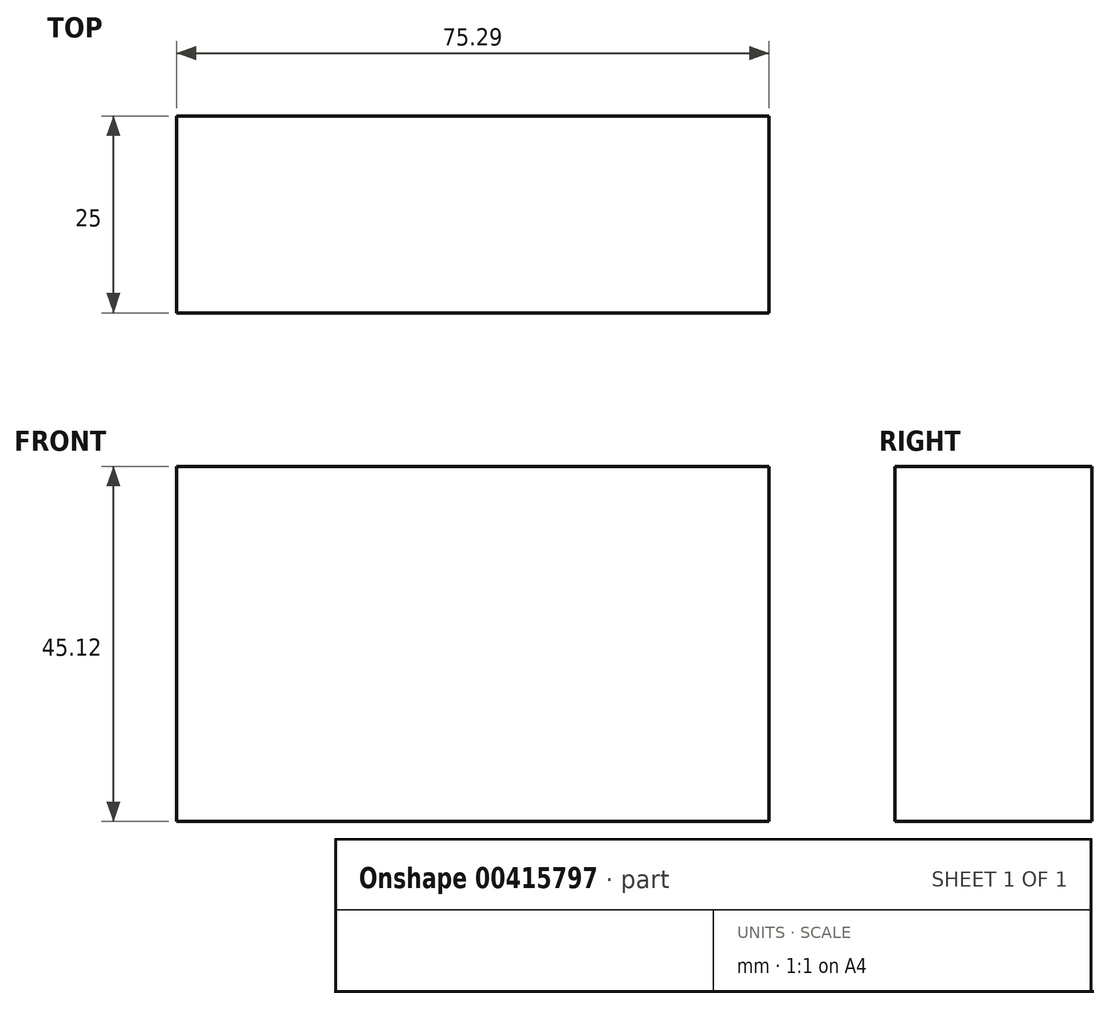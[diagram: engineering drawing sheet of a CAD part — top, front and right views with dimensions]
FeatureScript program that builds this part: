
annotation { "Feature Type Name" : "Feature", "Feature Type Description" : "" }
export const myFeature = defineFeature(function(context is Context, id is Id, definition is map)
    precondition{}
    {
        {
            var Q0;
            Q0=qCreatedBy(makeId("Front.planeOp"),FACE);
            var sketch = newSketch(context, id + "F0", { "sketchPlane" : qUnion([Q0])});
            skLineSegment(sketch, "E0.bottom", {"start": v(-100.61, 5.68) * mm, "end": v(-25.32, 5.68) * mm});
            skLineSegment(sketch, "E0.top", {"start": v(-100.61, -39.44) * mm, "end": v(-25.32, -39.44) * mm});
            skLineSegment(sketch, "E0.left", {"start": v(-100.61, 5.68) * mm, "end": v(-100.61, -39.44) * mm});
            skLineSegment(sketch, "E0.right", {"start": v(-25.32, 5.68) * mm, "end": v(-25.32, -39.44) * mm});
            skSolve(sketch);
        }
        {
            var Q0;
            Q0 = qSketchRegion(id + "F0", true);
            extrude(context, id + "F1", {"entities" : qUnion([Q0]), "depth" : 25 * mm});
        }
    });
